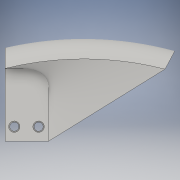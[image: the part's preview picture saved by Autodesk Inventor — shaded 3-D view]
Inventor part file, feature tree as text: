
AUTODESK INVENTOR PART (.ipt)
format: ipt  version: 2016 (Build 200138000, 138)  size: 929,280 bytes
history: native  units: in
note: dims shown in document units (in); Inventor stores cm internally (conversion verified against a paired STEP export)
features: sketch x5, extrude x2, other x2, sweep x1, loft x1, hole x1
ambient origin geometry x8: Origin, YZ Plane, XZ Plane, XY Plane, X Axis, Y Axis, Z Axis, Center Point
bodies: Solid1 (feature_tree)
feature tree (12):
  extrude  "Extrusion1"  Depth=0.5in
  extrude  "Extrusion2"  Depth=0.5in TaperAngle=0.0deg
  sketch  "Sketch4"  dims[d22=0.75in d23=0.0in d25=0.0125in]
  sketch  "Sketch6"  dims[d41=1.0in d42=0.0in d43=0.0in]
  sweep  "Sweep3"
  loft  "Loft1"
  hole  "Hole4"  [1 undecoded]
  sketch  "Sketch1"  dims[d0=0.75in d1=0.5in]
  sketch  "Sketch3"  dims[d2=0.4173in d3=0.5in d4=0.0in]
  other  "Edges1"
  other  "Edges2"
  sketch  "Sketch9"  dims[d44=0.0in d45=90.0deg d46=0.0in d47=90.0deg d48=0.1575in d49=0.75in d50=0.1969in d51=0.1181in d52=0.5635in d53=1.0in d54=0.8108in d5=1.0in d6=1.0in]
note: 1 required parameter value undecoded (feature->parameter linkage not recoverable at this tier; creation-order binding heuristic only, values carry confidence <= 0.55)
